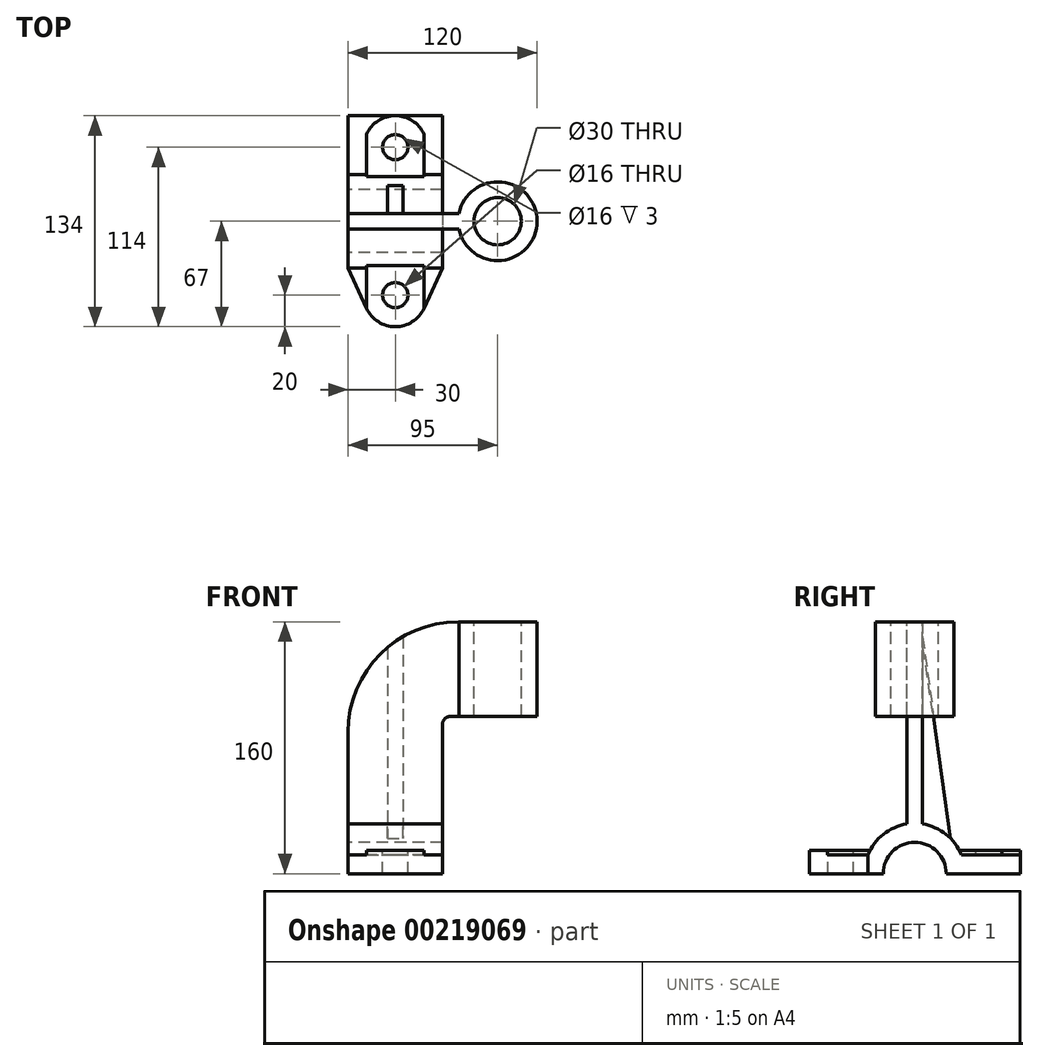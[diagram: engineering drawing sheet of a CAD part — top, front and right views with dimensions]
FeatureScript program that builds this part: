
annotation { "Feature Type Name" : "Feature", "Feature Type Description" : "" }
export const myFeature = defineFeature(function(context is Context, id is Id, definition is map)
    precondition{}
    {
        {
            var Q0;
            Q0=qCreatedBy(makeId("Right.planeOp"),FACE);
            var sketch = newSketch(context, id + "F0", { "sketchPlane" : qUnion([Q0])});
            skArc(sketch, "E0", {"start": v(32, 0) * mm, "mid": v(0, 32) * mm, "end": v(-32, 0) * mm});
            skArc(sketch, "E1", {"start": v(20, 0) * mm, "mid": v(0, 20) * mm, "end": v(-20, 0) * mm});
            skLineSegment(sketch, "E2", {"start": v(5, 31.6) * mm, "end": v(5, 160) * mm});
            skLineSegment(sketch, "E3", {"start": v(5, 160) * mm, "end": v(-5, 160) * mm});
            skLineSegment(sketch, "E4", {"start": v(-5, 160) * mm, "end": v(-5, 31.6) * mm});
            skLineSegment(sketch, "E5", {"start": v(32, 0) * mm, "end": v(20, 0) * mm});
            skLineSegment(sketch, "E6.trimOffspring", {"start": v(-20, 0) * mm, "end": v(-32, 0) * mm});
            skPoint(sketch, "E7.orphan", {"position": v(69.06, 0) * mm});
            skLineSegment(sketch, "E8", {"start": v(-32, 0) * mm, "end": v(-67, 0) * mm});
            skLineSegment(sketch, "E9", {"start": v(-67, 0) * mm, "end": v(-67, 12) * mm});
            skLineSegment(sketch, "E10", {"start": v(-67, 12) * mm, "end": v(-29.66, 12) * mm});
            skPoint(sketch, "E11", {"position": v(0, 20) * mm});
            skLineSegment(sketch, "E12.MirrorCS", {"start": v(67, 12) * mm, "end": v(29.66, 12) * mm});
            skLineSegment(sketch, "E13.MirrorCS", {"start": v(32, 0) * mm, "end": v(67, 0) * mm});
            skLineSegment(sketch, "E14.MirrorCS", {"start": v(67, 0) * mm, "end": v(67, 12) * mm});
            skSolve(sketch);
        }
        {
            var Q0;
            {var subQ0=sQuery(id+"F0.wireOp",EDGE,"E2");Q0=makeQuery(id+"F0.imprint","IMPRINT",FACE,{"disambiguationData":[TD([[makeQuery(id+"F0.imprint","IMPRINT",EDGE,{"derivedFrom":subQ0}),1.0]])]});}
            extrude(context, id + "F1", {"entities" : qUnion([Q0]), "depth" : 75 * mm});
        }
        {
            var Q0;
            Q0=makeQuery(id+"F0.imprint","IMPRINT",FACE,{"disambiguationData":[TD([[makeQuery(id+"F0.imprint","IMPRINT",EDGE,{"derivedFrom":sQuery(id+"F0.wireOp",EDGE,"E1")}),-1.0]])]});
            extrude(context, id + "F2", {"entities" : qUnion([Q0]), "operationType" : NewBodyOperationType.ADD, "depth" : 60 * mm});
        }
        {
            var Q0;
            {var subQ0=sQuery(id+"F0.wireOp",EDGE,"E8");Q0=makeQuery(id+"F0.imprint","IMPRINT",FACE,{"disambiguationData":[TD([[makeQuery(id+"F0.imprint","IMPRINT",EDGE,{"derivedFrom":subQ0}),-1.0]])]});}
            var Q1;
            {var subQ2=sQuery(id+"F0.wireOp",EDGE,"E12.MirrorCS");Q1=makeQuery(id+"F0.imprint","IMPRINT",FACE,{"disambiguationData":[TD([[makeQuery(id+"F0.imprint","IMPRINT",EDGE,{"derivedFrom":subQ2}),1.0]])]});}
            extrude(context, id + "F3", {"entities" : qUnion([Q0, Q1]), "operationType" : NewBodyOperationType.ADD, "depth" : 60 * mm});
        }
        {
            var Q0;
            Q0=makeQuery(id+"F1.opExtrude","CAP_VERTEX",VERTEX,{"disambiguationData":[OSD([sQuery(id+"F0.wireOp",EDGE,"E3"),sQuery(id+"F0.wireOp",EDGE,"E4")])],"isStart":false});
            var Q1;
            Q1=qCreatedBy(makeId("Top.planeOp"),FACE);
            cPlane(context, id + "F4", {"entities" : qUnion([Q0, Q1]), "cplaneType" : CPlaneType.PLANE_POINT, "offset" : 25 * mm, "width" : 150 * mm, "height" : 150 * mm});
        }
        {
            var Q0;
            Q0=qCreatedBy(id+"F4.planeOp",FACE);
            var sketch = newSketch(context, id + "F5", { "sketchPlane" : qUnion([Q0])});
            skCircle(sketch, "E15", {"center": v(95, 0) * mm, "radius": 25 * mm});
            skCircle(sketch, "E16", {"center": v(95, 0) * mm, "radius": 15 * mm});
            skSolve(sketch);
        }
        {
            var Q0;
            Q0=makeQuery(id+"F5.imprint","IMPRINT",FACE,{"disambiguationData":[TD([[makeQuery(id+"F5.imprint","IMPRINT",EDGE,{"derivedFrom":sQuery(id+"F5.wireOp",EDGE,"E15")}),1.0]])]});
            extrude(context, id + "F6", {"entities" : qUnion([Q0]), "operationType" : NewBodyOperationType.ADD, "oppositeDirection" : true, "depth" : 60 * mm});
        }
        {
            var Q0;
            Q0=makeQuery(id+"F1.opExtrude","SWEPT_FACE",FACE,{"disambiguationData":[OSD([sQuery(id+"F0.wireOp",EDGE,"E4")])]});
            var sketch = newSketch(context, id + "F7", { "sketchPlane" : qUnion([Q0])});
            skLineSegment(sketch, "E17", {"start": v(60, 100) * mm, "end": v(60, 31.6) * mm});
            skLineSegment(sketch, "E18.0", {"start": v(75, 100) * mm, "end": v(75, 31.6) * mm});
            skLineSegment(sketch, "E19.0", {"start": v(75, 31.6) * mm, "end": v(60, 31.6) * mm});
            skPoint(sketch, "E20.orphan", {"position": v(60, 31.6) * mm});
            skPoint(sketch, "E21.orphan", {"position": v(120, 100) * mm});
            skLineSegment(sketch, "E22", {"start": v(60, 100) * mm, "end": v(75, 100) * mm});
            skSolve(sketch);
        }
        {
            var Q0;
            Q0=makeQuery(id+"F7.imprint","IMPRINT",FACE,{"disambiguationData":[TD([[makeQuery(id+"F7.imprint","IMPRINT",EDGE,{"derivedFrom":sQuery(id+"F7.wireOp",EDGE,"E17")}),1.0]])]});
            extrude(context, id + "F8", {"entities" : qUnion([Q0]), "operationType" : NewBodyOperationType.REMOVE, "endBound" : BoundingType.UP_TO_NEXT, "oppositeDirection" : true, "depth" : 25 * mm});
        }
        {
            var Q0;
            Q0=makeQuery(id+"F8.boolean.opBoolean","COPY",EDGE,{"derivedFrom":makeQuery(id+"F8.opExtrude","SWEPT_EDGE",EDGE,{"disambiguationData":[OSD([sQuery(id+"F7.wireOp",EDGE,"E17"),sQuery(id+"F7.wireOp",EDGE,"E22")])]})});
            fillet(context, id + "F9", {"entities" : qUnion([Q0]), "radius" : 5 * mm, "tangentPropagation" : true, "allowEdgeOverflow" : false});
        }
        {
            var Q0;
            Q0=makeQuery(id+"F3.opExtrude","SWEPT_FACE",FACE,{"disambiguationData":[OSD([sQuery(id+"F0.wireOp",EDGE,"E10")])]});
            var sketch = newSketch(context, id + "F10", { "sketchPlane" : qUnion([Q0])});
            skArc(sketch, "E23", {"start": v(11.83, -55.36) * mm, "mid": v(30, -67) * mm, "end": v(48.17, -55.36) * mm});
            skCircle(sketch, "E24", {"center": v(30, -47) * mm, "radius": 8 * mm});
            skLineSegment(sketch, "E25", {"start": v(0, -29.66) * mm, "end": v(11.83, -55.36) * mm});
            skLineSegment(sketch, "E26", {"start": v(60, -29.66) * mm, "end": v(48.17, -55.36) * mm});
            skLineSegment(sketch, "E27.0", {"start": v(60, -67) * mm, "end": v(60, -29.66) * mm});
            skLineSegment(sketch, "E28.0", {"start": v(60, -67) * mm, "end": v(0, -67) * mm});
            skLineSegment(sketch, "E29.0", {"start": v(0, -67) * mm, "end": v(0, -29.66) * mm});
            skLineSegment(sketch, "E30", {"start": v(11.83, -29.66) * mm, "end": v(11.83, -55.36) * mm});
            skLineSegment(sketch, "E31", {"start": v(48.17, -55.36) * mm, "end": v(48.17, -29.66) * mm});
            skLineSegment(sketch, "E32.0", {"start": v(48.17, -20) * mm, "end": v(11.83, -20) * mm});
            skLineSegment(sketch, "E33", {"start": v(60, -29.66) * mm, "end": v(60, -20) * mm});
            skLineSegment(sketch, "E34", {"start": v(0, -29.66) * mm, "end": v(0, -20) * mm});
            skLineSegment(sketch, "E35", {"start": v(48.17, -29.66) * mm, "end": v(48.17, -20) * mm});
            skLineSegment(sketch, "E36", {"start": v(11.83, -29.66) * mm, "end": v(11.83, -20) * mm});
            skLineSegment(sketch, "E37", {"start": v(48.17, -24.83) * mm, "end": v(11.83, -24.83) * mm});
            skLineSegment(sketch, "E38.MirrorCS", {"start": v(48.17, 55.36) * mm, "end": v(48.17, 29.66) * mm});
            skLineSegment(sketch, "E39.MirrorCS", {"start": v(60, 29.66) * mm, "end": v(48.17, 55.36) * mm});
            skArc(sketch, "E40.MirrorCS", {"start": v(11.83, 55.36) * mm, "mid": v(30, 67) * mm, "end": v(48.17, 55.36) * mm});
            skLineSegment(sketch, "E41.MirrorCS", {"start": v(60, 67) * mm, "end": v(0, 67) * mm});
            skLineSegment(sketch, "E42.MirrorCS", {"start": v(60, 67) * mm, "end": v(60, 29.66) * mm});
            skLineSegment(sketch, "E43.MirrorCS", {"start": v(0, 67) * mm, "end": v(0, 29.66) * mm});
            skLineSegment(sketch, "E44.MirrorCS", {"start": v(0, 29.66) * mm, "end": v(11.83, 55.36) * mm});
            skLineSegment(sketch, "E45.MirrorCS", {"start": v(11.83, 29.66) * mm, "end": v(11.83, 55.36) * mm});
            skLineSegment(sketch, "E46.MirrorCS", {"start": v(48.17, 24.83) * mm, "end": v(11.83, 24.83) * mm});
            skLineSegment(sketch, "E47.MirrorCS", {"start": v(48.17, 29.66) * mm, "end": v(48.17, 20) * mm});
            skLineSegment(sketch, "E48.MirrorCS", {"start": v(11.83, 29.66) * mm, "end": v(11.83, 20) * mm});
            skLineSegment(sketch, "E49.MirrorCS", {"start": v(48.17, 20) * mm, "end": v(11.83, 20) * mm});
            skCircle(sketch, "E50.MirrorC", {"center": v(30, 47) * mm, "radius": 8 * mm});
            skSolve(sketch);
        }
        {
            var Q0;
            {var subQ0=sQuery(id+"F10.wireOp",EDGE,"E25");Q0=makeQuery(id+"F10.imprint","IMPRINT",FACE,{"disambiguationData":[TD([[makeQuery(id+"F10.imprint","IMPRINT",EDGE,{"derivedFrom":subQ0}),-1.0]])]});}
            var Q1;
            {var subQ0=sQuery(id+"F10.wireOp",EDGE,"E26");Q1=makeQuery(id+"F10.imprint","IMPRINT",FACE,{"disambiguationData":[TD([[makeQuery(id+"F10.imprint","IMPRINT",EDGE,{"derivedFrom":subQ0}),1.0]])]});}
            var Q2;
            Q2=makeQuery(id+"F10.imprint","IMPRINT",FACE,{"disambiguationData":[TD([[makeQuery(id+"F10.imprint","IMPRINT",EDGE,{"derivedFrom":sQuery(id+"F10.wireOp",EDGE,"E24")}),1.0]])]});
            extrude(context, id + "F11", {"entities" : qUnion([Q0, Q1, Q2]), "operationType" : NewBodyOperationType.REMOVE, "oppositeDirection" : true, "depth" : 25 * mm});
        }
        {
            var Q0;
            Q0=makeQuery(id+"F10.imprint","IMPRINT",FACE,{"disambiguationData":[TD([[makeQuery(id+"F10.imprint","IMPRINT",EDGE,{"derivedFrom":sQuery(id+"F10.wireOp",EDGE,"E24")}),-1.0]])]});
            cPlane(context, id + "F12", {"entities" : qUnion([Q0]), "cplaneType" : CPlaneType.OFFSET, "offset" : 3 * mm, "width" : 150 * mm, "height" : 150 * mm});
        }
        {
            var Q0;
            Q0=qCreatedBy(id+"F12.planeOp",FACE);
            var sketch = newSketch(context, id + "F13", { "sketchPlane" : qUnion([Q0])});
            skLineSegment(sketch, "E51.0", {"start": v(48.17, -55.36) * mm, "end": v(48.17, -29.66) * mm});
            skLineSegment(sketch, "E52.0", {"start": v(48.17, -29.66) * mm, "end": v(48.17, -20) * mm});
            skLineSegment(sketch, "E53.0", {"start": v(48.17, -20) * mm, "end": v(11.83, -20) * mm});
            skLineSegment(sketch, "E54.0", {"start": v(11.83, -29.66) * mm, "end": v(11.83, -20) * mm});
            skLineSegment(sketch, "E55.0", {"start": v(11.83, -29.66) * mm, "end": v(11.83, -55.36) * mm});
            skArc(sketch, "E56.0", {"start": v(11.83, -55.36) * mm, "mid": v(30, -67) * mm, "end": v(48.17, -55.36) * mm});
            skCircle(sketch, "E57.0", {"center": v(30, -47) * mm, "radius": 8 * mm});
            skLineSegment(sketch, "E58.MirrorCS", {"start": v(11.83, 29.66) * mm, "end": v(11.83, 55.36) * mm});
            skLineSegment(sketch, "E59.MirrorCS", {"start": v(48.17, 55.36) * mm, "end": v(48.17, 29.66) * mm});
            skArc(sketch, "E60.MirrorCS", {"start": v(11.83, 55.36) * mm, "mid": v(30, 67) * mm, "end": v(48.17, 55.36) * mm});
            skLineSegment(sketch, "E61.MirrorCS", {"start": v(48.17, 20) * mm, "end": v(11.83, 20) * mm});
            skLineSegment(sketch, "E62.MirrorCS", {"start": v(48.17, 29.66) * mm, "end": v(48.17, 20) * mm});
            skLineSegment(sketch, "E63.MirrorCS", {"start": v(11.83, 29.66) * mm, "end": v(11.83, 20) * mm});
            skCircle(sketch, "E64.MirrorC", {"center": v(30, 47) * mm, "radius": 8 * mm});
            skSolve(sketch);
        }
        {
            var Q0;
            Q0 = qSketchRegion(id + "F13", true);
            var Q1;
            Q1=makeQuery(id+"F3.boolean.opBoolean","MERGE",FACE,{"derivedFrom":[makeQuery(id+"F2.opExtrude","SWEPT_FACE",FACE,{"disambiguationData":[OSD([sQuery(id+"F0.wireOp",EDGE,"E6.trimOffspring")])]}),makeQuery(id+"F3.opExtrude","SWEPT_FACE",FACE,{"disambiguationData":[OSD([sQuery(id+"F0.wireOp",EDGE,"E8")])]})]});
            extrude(context, id + "F14", {"entities" : qUnion([Q0]), "operationType" : NewBodyOperationType.ADD, "endBound" : BoundingType.UP_TO_SURFACE, "oppositeDirection" : true, "endBoundEntityFace" : qUnion([Q1]), "depth" : 5 * mm});
        }
        {
            var Q0;
            {var subQ0=sQuery(id+"F0.wireOp",EDGE,"E0");Q0=makeQuery(id+"F8.boolean.opBoolean","MERGE",FACE,{"derivedFrom":[makeQuery(id+"F3.boolean.opBoolean","MERGE",FACE,{"derivedFrom":[makeQuery(id+"F2.opExtrude","CAP_FACE",FACE,{"disambiguationData":[OSD([subQ0,sQuery(id+"F0.wireOp",EDGE,"E1"),sQuery(id+"F0.wireOp",EDGE,"E5"),sQuery(id+"F0.wireOp",EDGE,"E6.trimOffspring")])],"isStart":false}),makeQuery(id+"F3.opExtrude","CAP_FACE",FACE,{"disambiguationData":[OSD([subQ0,sQuery(id+"F0.wireOp",EDGE,"E12.MirrorCS"),sQuery(id+"F0.wireOp",EDGE,"E13.MirrorCS"),sQuery(id+"F0.wireOp",EDGE,"E14.MirrorCS")])],"isStart":false}),makeQuery(id+"F3.opExtrude","CAP_FACE",FACE,{"disambiguationData":[OSD([subQ0,sQuery(id+"F0.wireOp",EDGE,"E8"),sQuery(id+"F0.wireOp",EDGE,"E9"),sQuery(id+"F0.wireOp",EDGE,"E10")])],"isStart":false})]}),makeQuery(id+"F8.opExtrude","SWEPT_FACE",FACE,{"disambiguationData":[OSD([sQuery(id+"F7.wireOp",EDGE,"E17")])]})]});}
            var sketch = newSketch(context, id + "F15", { "sketchPlane" : qUnion([Q0])});
            skArc(sketch, "E65.0", {"start": v(20, 0) * mm, "mid": v(0, 20) * mm, "end": v(-20, 0) * mm});
            skLineSegment(sketch, "E66", {"start": v(-20, 0) * mm, "end": v(20, 0) * mm});
            skSolve(sketch);
        }
        {
            var Q0;
            Q0=makeQuery(id+"F15.imprint","IMPRINT",FACE,{"disambiguationData":[TD([[makeQuery(id+"F15.imprint","IMPRINT",EDGE,{"derivedFrom":sQuery(id+"F15.wireOp",EDGE,"E65.0")}),1.0]])]});
            extrude(context, id + "F16", {"entities" : qUnion([Q0]), "operationType" : NewBodyOperationType.REMOVE, "endBound" : BoundingType.THROUGH_ALL, "oppositeDirection" : true, "depth" : 25 * mm});
        }
        {
            var Q0;
            Q0=qCreatedBy(makeId("Right.planeOp"),FACE);
            cPlane(context, id + "F17", {"entities" : qUnion([Q0]), "cplaneType" : CPlaneType.OFFSET, "offset" : 25 * mm, "width" : 150 * mm, "height" : 150 * mm});
        }
        {
            var Q0;
            Q0=makeQuery(id+"F1.opExtrude","CAP_EDGE",EDGE,{"disambiguationData":[OSD([sQuery(id+"F0.wireOp",EDGE,"E3")])],"isStart":true});
            fillet(context, id + "F18", {"entities" : qUnion([Q0]), "radius" : 70 * mm, "tangentPropagation" : true, "allowEdgeOverflow" : false});
        }
        {
            var Q0;
            Q0=qCreatedBy(id+"F17.planeOp",FACE);
            var sketch = newSketch(context, id + "F19", { "sketchPlane" : qUnion([Q0])});
            skLineSegment(sketch, "E67", {"start": v(5, 143.62) * mm, "end": v(5, 31.6) * mm});
            skArc(sketch, "E68", {"start": v(5, 31.6) * mm, "mid": v(18.6, 26.05) * mm, "end": v(28.27, 15) * mm});
            skLineSegment(sketch, "E69", {"start": v(5, 143.62) * mm, "end": v(22.79, 22.47) * mm});
            skSolve(sketch);
        }
        {
            var Q0;
            Q0=qCreatedBy(id+"F17.planeOp",FACE);
            cPlane(context, id + "F20", {"entities" : qUnion([Q0]), "cplaneType" : CPlaneType.OFFSET, "offset" : 10 * mm, "width" : 150 * mm, "height" : 150 * mm});
        }
        {
            var Q0;
            Q0=qCreatedBy(id+"F20.planeOp",FACE);
            var sketch = newSketch(context, id + "F21", { "sketchPlane" : qUnion([Q0])});
            skLineSegment(sketch, "E70", {"start": v(5, 150.62) * mm, "end": v(5, 31.6) * mm});
            skPoint(sketch, "E71.0", {"position": v(22.79, 22.47) * mm});
            skArc(sketch, "E72.0", {"start": v(5, 31.6) * mm, "mid": v(14.63, 28.46) * mm, "end": v(22.79, 22.47) * mm});
            skLineSegment(sketch, "E73", {"start": v(5, 150.62) * mm, "end": v(22.79, 22.47) * mm});
            skPoint(sketch, "E74.orphan", {"position": v(28.27, 15) * mm});
            skSolve(sketch);
        }
        {
            var Q1;
            Q1 = qSketchRegion(id + "F19", true);
            var Q2;
            Q2 = qSketchRegion(id + "F21", true);
            var Q3;
            Q3=sQuery(id+"F19.wireOp",VERTEX,"E67.start");
            loft(context, id + "F22", {"operationType" : NewBodyOperationType.ADD, "sheetProfilesArray" : [{ "sheetProfileEntities" : qUnion([Q1]) }, { "sheetProfileEntities" : qUnion([Q2]) }], "connections" : [{ "connectionEntities" : qUnion([Q3]), "connectionEdgeQueries" : qUnion([]), "connectionEdgeParameters" : [] }]});
        }
    });
